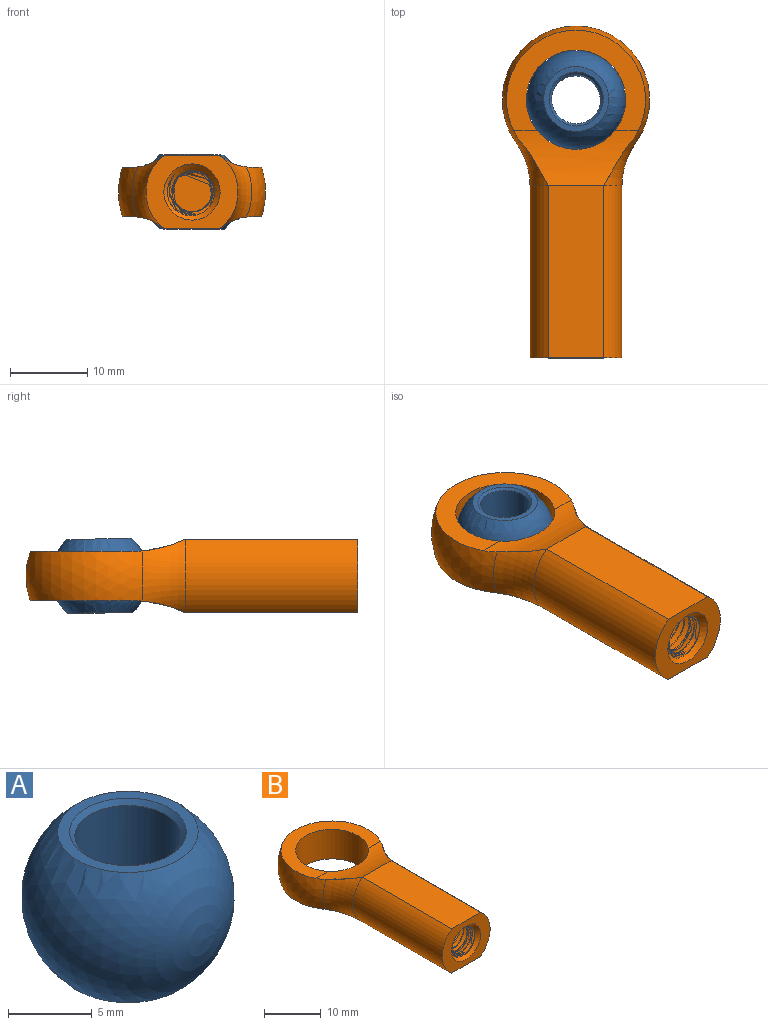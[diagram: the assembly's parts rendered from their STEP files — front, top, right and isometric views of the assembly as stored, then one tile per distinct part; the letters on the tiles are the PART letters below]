
ASSEMBLY  parts=2 mates=1
PART A: 6 faces, bbox 12.7x12.7x12.7 mm
  f0: sphere r=6.35mm, area 380mm2, adj f1,f2
  f1: plane 8.4x8.4mm, normal (0,0,1), area 17.1mm2, adj f0,f5
  f2: plane 8.4x8.4mm, normal (0,0,-1), area 17.1mm2, adj f0,f4
  f3: cylinder r=3.17mm len=8.89mm, axis (0,0,1), area 177.3mm2, adj f4,f5
  f4: cone r=3.49mm half-angle=45deg, axis (0,0,-1), area 9.4mm2, adj f2,f3
  f5: cone r=3.49mm half-angle=45deg, axis (0,0,1), area 9.4mm2, adj f1,f3
PART B: 19 faces, bbox 19.7x43.6x19.7 mm
  f0: torus R=15.47mm, axis (0,-1,0), area 52.1mm2, adj f2,f13,f16,f17
  f1: plane 11.89x9.53mm, normal (0,-1,0), area 58.2mm2, adj f2,f3,f4,f10,f11
  f2: cylinder r=5.94mm len=22.22mm, axis (0,1,0), area 245.5mm2, adj f0,f1,f10,f11
  f3: cylinder r=5.94mm len=22.22mm, axis (0,1,0), area 245.5mm2, adj f1,f10,f11,f12
  f4: cone r=3.63mm half-angle=45deg, axis (0,-1,0), area 21.4mm2, adj f1,f6,f7,f8,f9
  f5: plane 6.15x6.13mm, normal (0,-1,0), area 26.2mm2, adj f6,f7,f8,f9
  f6: bspline ~17.35x6.35mm, area 227.2mm2, adj f4,f5,f7,f9
  f7: bspline ~16.78x5.17mm, area 33.3mm2, adj f4,f5,f6,f8
  f8: bspline ~17.91x6.35mm, area 226.8mm2, adj f4,f5,f7,f9
  f9: cylinder r=3.17mm len=17.01mm, axis (0,-1,0), area 30.2mm2, adj f4,f5,f6,f8
  f10: plane 22.22x7.11mm, normal (0,0,1), area 158mm2, adj f1,f2,f3,f16
  f11: plane 22.22x7.11mm, normal (0,0,-1), area 158mm2, adj f1,f2,f3,f17
  f12: torus R=15.47mm, axis (0,-1,0), area 52.1mm2, adj f3,f13,f16,f17
  f13: sphere r=9.53mm, area 269.5mm2, adj f0,f12,f14,f15,f16,f17
  f14: plane 17.96x13mm, normal (0,0,1), area 83.8mm2, adj f13,f16,f18
  f15: plane 18.66x13.7mm, normal (0,0,-1), area 83.8mm2, adj f13,f17,f18
  f16: cylinder r=16.67mm len=16.06mm, axis (-1,0,0), area 67.8mm2, adj f0,f10,f12,f13,f14,f18
  f17: cylinder r=16.67mm len=16.06mm, axis (1,0,0), area 67.8mm2, adj f0,f11,f12,f13,f15,f18
  f18: cylinder r=6.41mm len=12.83mm, axis (0,0,1), area 255.9mm2, adj f14,f15,f16,f17
PLACE A rot(axis=(-0.36,0.14,0.92),3deg) t=(-14.36,-8.38,10.16)mm
PLACE B t=(-15.14,-8.4,9.86)mm fixed
MATE ball B.f18 <-> A.f3  axis (0,0,1) through (-15.14,7.48,9.86)mm
